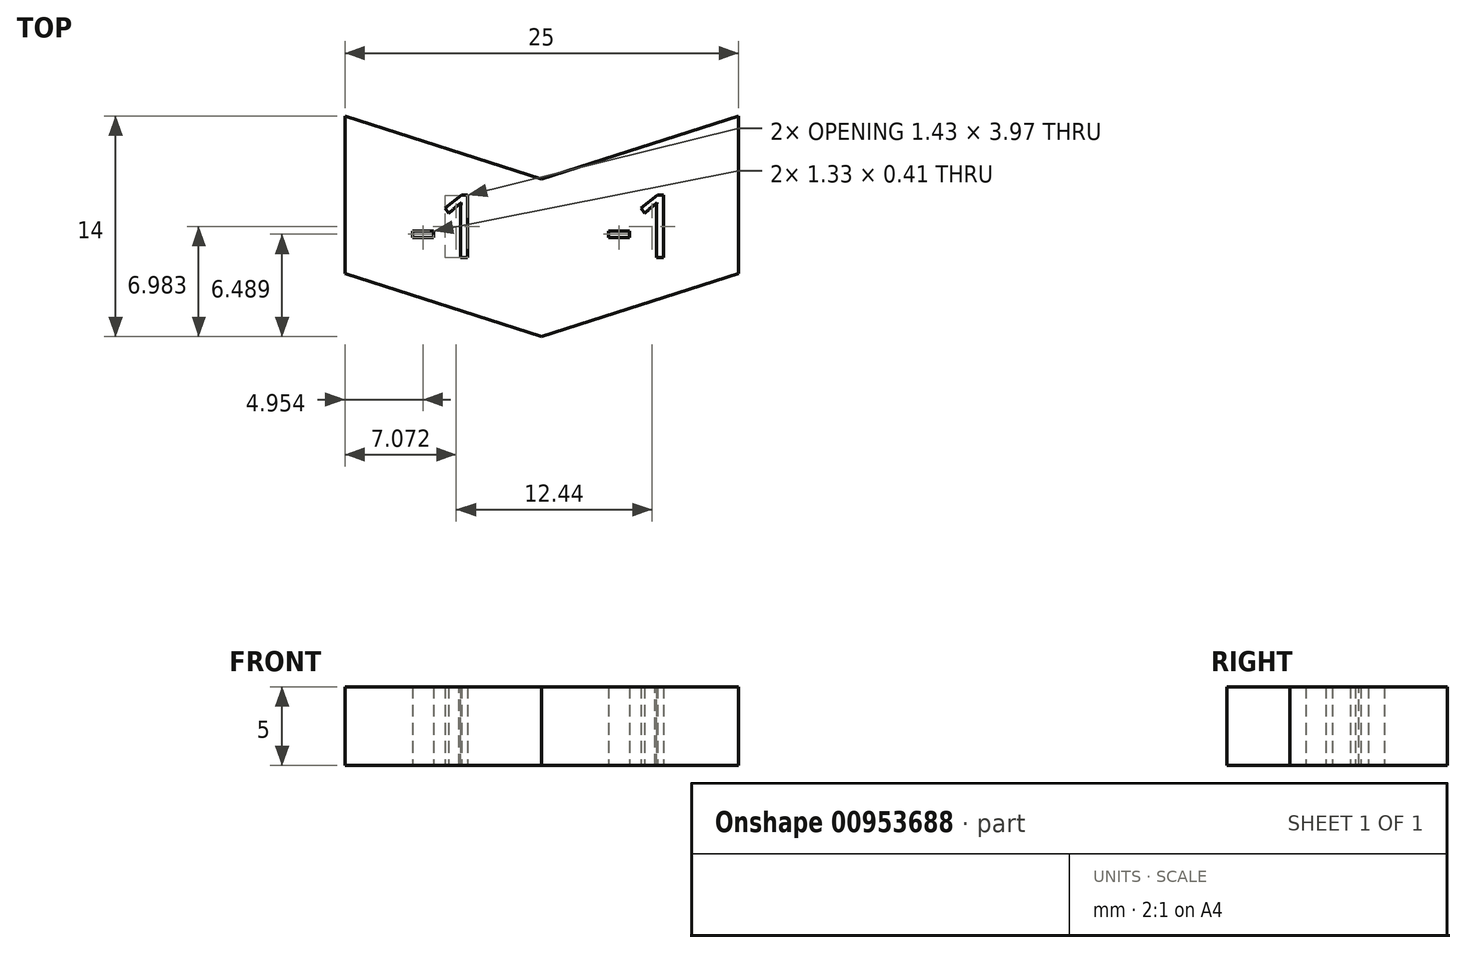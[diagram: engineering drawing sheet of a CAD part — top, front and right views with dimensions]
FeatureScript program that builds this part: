
annotation { "Feature Type Name" : "Feature", "Feature Type Description" : "" }
export const myFeature = defineFeature(function(context is Context, id is Id, definition is map)
    precondition{}
    {
        {
            var Q0;
            Q0=qCreatedBy(makeId("Top.planeOp"),FACE);
            var sketch = newSketch(context, id + "F0", { "sketchPlane" : qUnion([Q0])});
            skLineSegment(sketch, "E0.bottom", {"start": v(0, 20) * mm, "end": v(25, 20) * mm, "construction": true});
            skLineSegment(sketch, "E0.top", {"start": v(0, 0) * mm, "end": v(25, 0) * mm, "construction": true});
            skLineSegment(sketch, "E1", {"start": v(0, 0) * mm, "end": v(0, 10) * mm});
            skLineSegment(sketch, "E2", {"start": v(25, 0) * mm, "end": v(25, 10) * mm});
            skLineSegment(sketch, "E3", {"start": v(12.5, 0) * mm, "end": v(12.5, 14) * mm, "construction": true});
            skLineSegment(sketch, "E4", {"start": v(12.5, 14) * mm, "end": v(12.5, 4) * mm, "construction": true});
            skText(sketch, "E5", { "text": "-1", "fontName": "OpenSans-Regular.ttf"});
            skLineSegment(sketch, "E6", {"start": v(0, 0) * mm, "end": v(4, 0) * mm, "construction": true});
            skLineSegment(sketch, "E7", {"start": v(4, 0) * mm, "end": v(4.06, 5) * mm, "construction": true});
            skLineSegment(sketch, "E8", {"start": v(16.5, 0) * mm, "end": v(16.5, 5) * mm, "construction": true});
            skText(sketch, "E9", { "text": "-1", "fontName": "OpenSans-Regular.ttf"});
            skLineSegment(sketch, "E10", {"start": v(20.59, 7) * mm, "end": v(4.06, 7) * mm, "construction": true});
            skLineSegment(sketch, "E11.MirrorCS", {"start": v(12.5, 0) * mm, "end": v(0, 4) * mm});
            skLineSegment(sketch, "E12.MirrorCS", {"start": v(0, 14) * mm, "end": v(0, 4) * mm});
            skLineSegment(sketch, "E13.MirrorCS", {"start": v(0, 14) * mm, "end": v(12.5, 10) * mm});
            skLineSegment(sketch, "E14.MirrorCS", {"start": v(12.5, 10) * mm, "end": v(25, 14) * mm});
            skLineSegment(sketch, "E15.MirrorCS", {"start": v(25, 4) * mm, "end": v(12.5, 0) * mm});
            skLineSegment(sketch, "E16.MirrorCS", {"start": v(25, 14) * mm, "end": v(25, 4) * mm});
            const initialGuessF0  = {"E5": [0.00406, 0.005, 1, 0, 0.004], "E9": [0.0165, 0.005, 1, 0, 0.004]};
            skSetInitialGuess(sketch, initialGuessF0);
            skSolve(sketch);
        }
        {
            var Q0;
            Q0=makeQuery(id+"F0.imprint","IMPRINT",FACE,{"disambiguationData":[TD([[makeQuery(id+"F0.imprint","IMPRINT",EDGE,{"derivedFrom":sQuery(id+"F0.wireOp",EDGE,"E5.sketch_text.stroke-0")}),1.0]])]});
            extrude(context, id + "F1", {"entities" : qUnion([Q0]), "depth" : 5 * mm, "offsetDistance" : 25 * mm});
        }
    });
